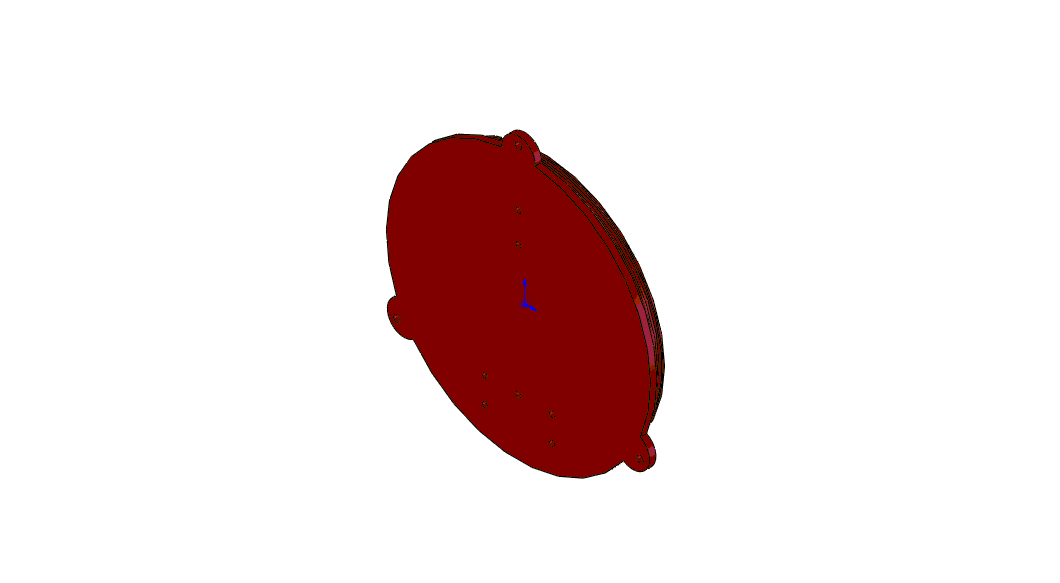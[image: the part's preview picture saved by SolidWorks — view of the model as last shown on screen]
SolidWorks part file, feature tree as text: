
SOLIDWORKS PART (.sldprt)
format: sldprt  version: not decoded by parser v0  size: 310,272 bytes
history: native  units: mm
features: sketch x12, extrude x3, hole x3, material x1, cut_extrude x1, cut_revolve x1, chamfer x1 (+11 scaffold rows collapsed)
feature tree (33):
  scaffold x11  (default folders/planes/origin — collapsed)
  material  "6061 Alloy"
  sketch  "Sketch1"  dims[D1=98.425mm]
  extrude  "Extrude1"  Depth=4.7625mm
  sketch  "Sketch2"  dims[D1=88.9mm]
  extrude  "Extrude2"  Depth=12.7mm
  sketch  "Sketch3"  dims[D1=82.55mm]
  cut_extrude  "Cut-Extrude1"  Depth=12.7mm
  sketch  "Sketch4"  dims[D1=2.54mm D2=3.175mm]
  cut_revolve  "Cut-Revolve1"  Angle=360deg
  sketch  "Sketch5"  dims[c1.D1=93.6625mm c1.D3=12.7mm c1.D4=12.7mm c1.D5=12.7mm c2.D1=150.0deg c3.D1=~86.613366mm c4.D1=120.0deg c4.D2=100.0125mm c5.D2=120.0deg]
  extrude  "Extrude3"  [1 undecoded]
  sketch  "Sketch7"  dims[D1=30.0deg]
  hole  "#10 (0.1935) Diameter Hole1"  Diameter=4.9149mm Depth=330.2mm
  sketch  "3DSketch1"  dims[D1=106.3625mm D2=106.3625mm D3=106.3625mm]
  sketch  "Sketch8"  dims[hole-wizard template sketch: 47 standard entries collapsed; hole parameters kept: c15.Hole Depth=330.2mm c15.D3=~14.816244mm c15.Drill Angle=118.0deg]
  chamfer  "Chamfer1"  Distance=0.508mm Angle=45deg
  hole  "#6 Clearance Hole1"  Diameter=3.7973mm Depth=6.35mm
  sketch  "3DSketch2"  dims[c1.D1=~76.076938mm c1.D2=98.25mm c2.D2=~22.74186mm c2.D5=22.6mm c2.D3=~32.481641mm c2.D1=38.1mm c2.D4=~65.135618mm c3.D1=57.15mm c4.D1=22.606mm c4.D2=98.298mm c4.D3=57.15mm]
  sketch  "Sketch9"  dims[hole-wizard template sketch: 50 standard entries collapsed; hole parameters above]
  hole  "#6 Clearance Hole2"  Diameter=3.7973mm Depth=25.4mm
  sketch  "3DSketch3"  dims[c1.D1=~15.431718mm c1.D2=19.05mm c2.D2=~61.252051mm c2.D9=50.8mm c2.D3=~29.073908mm c2.D1=25.4mm c2.D4=~52.448176mm c3.D2=57.15mm c3.D5=19.05mm c3.D6=50.8mm c3.D7=25.4mm c3.D8=57.15mm]
  sketch  "Sketch10"  dims[hole-wizard template sketch: 50 standard entries collapsed; hole parameters above]
decode coverage: 20 of 21 modeling features carry decoded parameters
note: ~ marks probable driven/reference dimensions
note: 1 parameter value undecoded
note: suppression state not decoded; provenance and decode notes live in map.json
